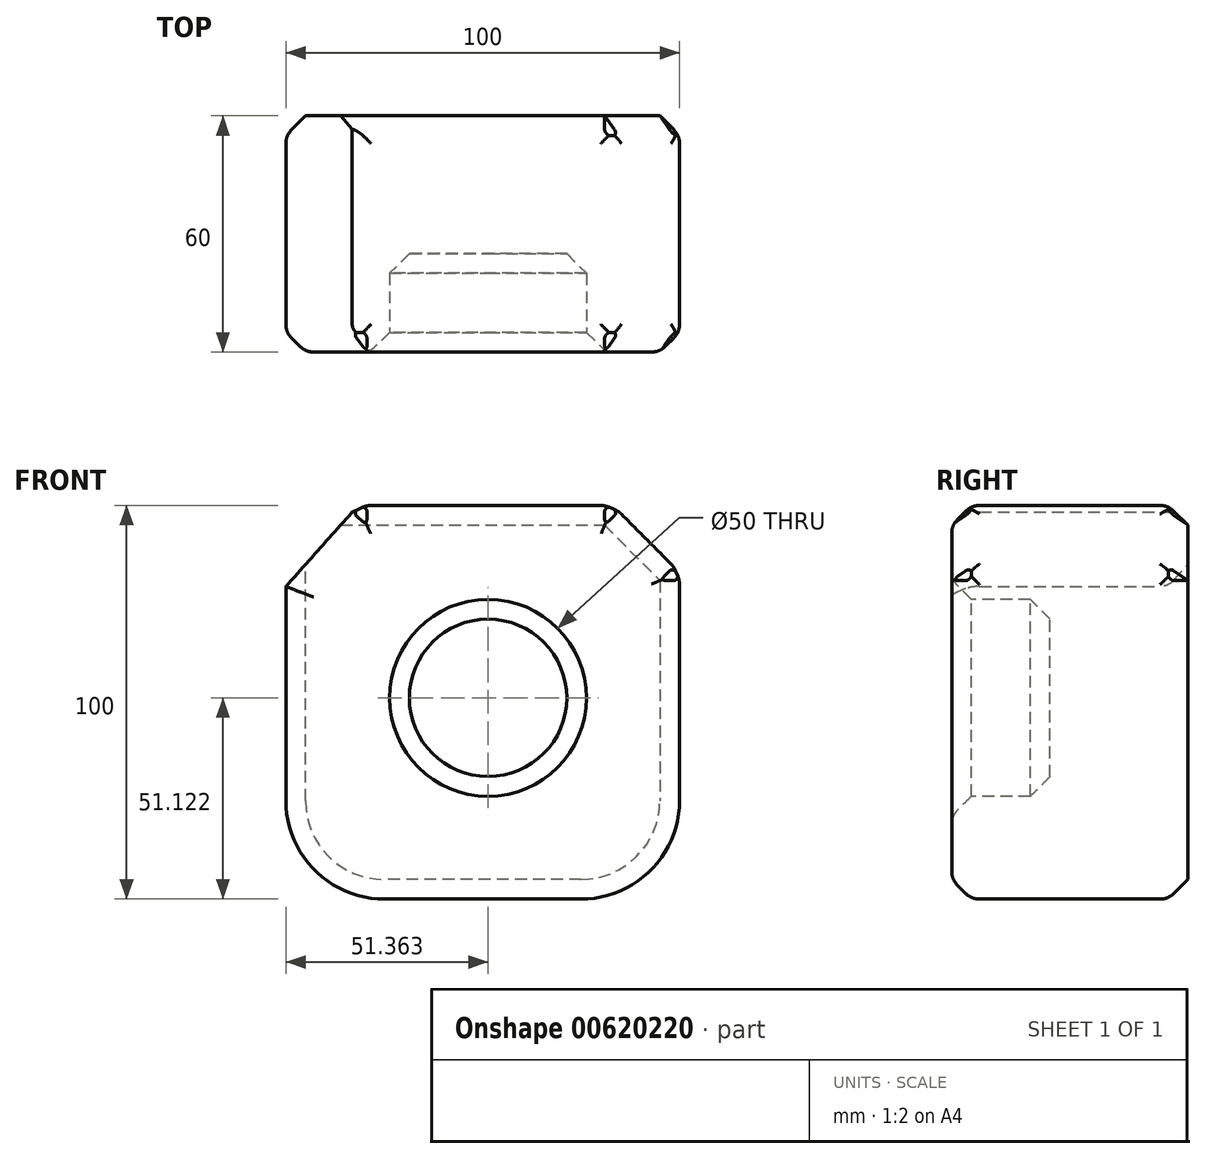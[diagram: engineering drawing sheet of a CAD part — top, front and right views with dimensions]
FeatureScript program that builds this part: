
annotation { "Feature Type Name" : "Feature", "Feature Type Description" : "" }
export const myFeature = defineFeature(function(context is Context, id is Id, definition is map)
    precondition{}
    {
        {
            var Q0;
            Q0=qCreatedBy(makeId("Front.planeOp"),FACE);
            var sketch = newSketch(context, id + "F0", { "sketchPlane" : qUnion([Q0])});
            skLineSegment(sketch, "E0.bottom", {"start": v(-23.76, 55.29) * mm, "end": v(40.98, 55.29) * mm});
            skLineSegment(sketch, "E0.top", {"start": v(-17.1, -44.71) * mm, "end": v(32.9, -44.71) * mm});
            skLineSegment(sketch, "E0.left", {"start": v(-42.1, 34.72) * mm, "end": v(-42.1, -19.71) * mm});
            skLineSegment(sketch, "E0.right", {"start": v(57.9, 38.27) * mm, "end": v(57.9, -19.71) * mm});
            skPoint(sketch, "E1.visualSharp", {"position": v(-42.1, -44.71) * mm});
            skArc(sketch, "E1.filletArc", {"start": v(-42.1, -19.71) * mm, "mid": v(-34.78, -37.39) * mm, "end": v(-17.1, -44.71) * mm});
            skPoint(sketch, "E2.visualSharp", {"position": v(57.9, -44.71) * mm});
            skArc(sketch, "E2.filletArc", {"start": v(32.9, -44.71) * mm, "mid": v(50.57, -37.39) * mm, "end": v(57.9, -19.71) * mm});
            skLineSegment(sketch, "E3", {"start": v(40.98, 55.29) * mm, "end": v(57.9, 38.27) * mm});
            skPoint(sketch, "E4.orphan", {"position": v(-42.1, 55.29) * mm});
            skPoint(sketch, "E5.orphan", {"position": v(-46.37, 38.27) * mm});
            skLineSegment(sketch, "E6", {"start": v(-23.76, 55.29) * mm, "end": v(-42.1, 34.72) * mm});
            skSolve(sketch);
        }
        {
            var Q0;
            Q0 = qSketchRegion(id + "F0", true);
            extrude(context, id + "F1", {"entities" : qUnion([Q0]), "depth" : 60 * mm, "offsetDistance" : 25 * mm});
        }
        {
            var Q0;
            Q0=makeQuery(id+"F1.opExtrude","CAP_FACE",FACE,{"disambiguationData":[OSD([sQuery(id+"F0.wireOp",EDGE,"E0.bottom"),sQuery(id+"F0.wireOp",EDGE,"E0.top"),sQuery(id+"F0.wireOp",EDGE,"E0.left"),sQuery(id+"F0.wireOp",EDGE,"E0.right"),sQuery(id+"F0.wireOp",EDGE,"E1.filletArc"),sQuery(id+"F0.wireOp",EDGE,"E2.filletArc"),sQuery(id+"F0.wireOp",EDGE,"E3"),sQuery(id+"F0.wireOp",EDGE,"E6")])],"isStart":false});
            var Q1;
            Q1=makeQuery(id+"F1.opExtrude","SWEPT_FACE",FACE,{"disambiguationData":[OSD([sQuery(id+"F0.wireOp",EDGE,"E0.bottom")])]});
            var Q2;
            Q2=makeQuery(id+"F1.opExtrude","SWEPT_FACE",FACE,{"disambiguationData":[OSD([sQuery(id+"F0.wireOp",EDGE,"E3")])]});
            var Q3;
            Q3=makeQuery(id+"F1.opExtrude","SWEPT_FACE",FACE,{"disambiguationData":[OSD([sQuery(id+"F0.wireOp",EDGE,"E0.right")])]});
            var Q4;
            Q4=makeQuery(id+"F1.opExtrude","SWEPT_FACE",FACE,{"disambiguationData":[OSD([sQuery(id+"F0.wireOp",EDGE,"E2.filletArc")])]});
            chamfer(context, id + "F2", {"entities" : qUnion([Q0, Q1, Q2, Q3, Q4]), "width" : 5 * mm, "tangentPropagation" : true});
        }
        {
            var Q0;
            Q0=makeQuery(id+"F1.opExtrude","CAP_FACE",FACE,{"disambiguationData":[OSD([sQuery(id+"F0.wireOp",EDGE,"E0.bottom"),sQuery(id+"F0.wireOp",EDGE,"E0.top"),sQuery(id+"F0.wireOp",EDGE,"E0.left"),sQuery(id+"F0.wireOp",EDGE,"E0.right"),sQuery(id+"F0.wireOp",EDGE,"E1.filletArc"),sQuery(id+"F0.wireOp",EDGE,"E2.filletArc"),sQuery(id+"F0.wireOp",EDGE,"E3"),sQuery(id+"F0.wireOp",EDGE,"E6")])],"isStart":false});
            var sketch = newSketch(context, id + "F3", { "sketchPlane" : qUnion([Q0])});
            skCircle(sketch, "E7", {"center": v(9.26, 6.41) * mm, "radius": 25 * mm});
            skSolve(sketch);
        }
        {
            var Q0;
            Q0=makeQuery(id+"F3.imprint","IMPRINT",FACE,{"disambiguationData":[TD([[makeQuery(id+"F3.imprint","IMPRINT",EDGE,{"derivedFrom":sQuery(id+"F3.wireOp",EDGE,"E7")}),1.0]])]});
            extrude(context, id + "F4", {"entities" : qUnion([Q0]), "operationType" : NewBodyOperationType.REMOVE, "oppositeDirection" : true, "depth" : 25 * mm, "offsetDistance" : 25 * mm});
        }
        {
            var Q0;
            Q0=makeQuery(id+"F4.boolean.opBoolean","COPY",FACE,{"derivedFrom":makeQuery(id+"F4.opExtrude","SWEPT_FACE",FACE,{"disambiguationData":[OSD([sQuery(id+"F3.wireOp",EDGE,"E7")])]})});
            chamfer(context, id + "F5", {"entities" : qUnion([Q0]), "width" : 5 * mm, "tangentPropagation" : true});
        }
        {
            var Q0;
            Q0=makeQuery(id+"F1.opExtrude","CAP_FACE",FACE,{"disambiguationData":[OSD([sQuery(id+"F0.wireOp",EDGE,"E0.bottom"),sQuery(id+"F0.wireOp",EDGE,"E0.top"),sQuery(id+"F0.wireOp",EDGE,"E0.left"),sQuery(id+"F0.wireOp",EDGE,"E0.right"),sQuery(id+"F0.wireOp",EDGE,"E1.filletArc"),sQuery(id+"F0.wireOp",EDGE,"E2.filletArc"),sQuery(id+"F0.wireOp",EDGE,"E3"),sQuery(id+"F0.wireOp",EDGE,"E6")])],"isStart":false});
            var Q1;
            Q1=makeQuery(id+"F1.opExtrude","SWEPT_FACE",FACE,{"disambiguationData":[OSD([sQuery(id+"F0.wireOp",EDGE,"E0.bottom")])]});
            var Q2;
            Q2=makeQuery(id+"F1.opExtrude","SWEPT_FACE",FACE,{"disambiguationData":[OSD([sQuery(id+"F0.wireOp",EDGE,"E3")])]});
            var Q3;
            Q3=makeQuery(id+"F1.opExtrude","SWEPT_FACE",FACE,{"disambiguationData":[OSD([sQuery(id+"F0.wireOp",EDGE,"E0.right")])]});
            var Q4;
            Q4=makeQuery(id+"F1.opExtrude","SWEPT_FACE",FACE,{"disambiguationData":[OSD([sQuery(id+"F0.wireOp",EDGE,"E2.filletArc")])]});
            var Q5;
            {var subQ0=sQuery(id+"F0.wireOp",EDGE,"E6");Q5=makeQuery(id+"F2.opChamfer","BLEND_EDGE",EDGE,{"blendedFrom":[makeQuery(id+"F1.opExtrude","CAP_EDGE",EDGE,{"disambiguationData":[OSD([subQ0])],"isStart":false}),makeQuery(id+"F1.opExtrude","SWEPT_FACE",FACE,{"disambiguationData":[OSD([subQ0])]})],"blendedInto":[makeQuery(id+"F1.opExtrude","SWEPT_FACE",FACE,{"disambiguationData":[OSD([subQ0])]})]});}
            fillet(context, id + "F6", {"entities" : qUnion([Q0, Q1, Q2, Q3, Q4, Q5]), "radius" : 5 * mm, "tangentPropagation" : true, "rho" : 0.5, "crossSection" : FilletCrossSection.CONIC, "allowEdgeOverflow" : false});
        }
    });
